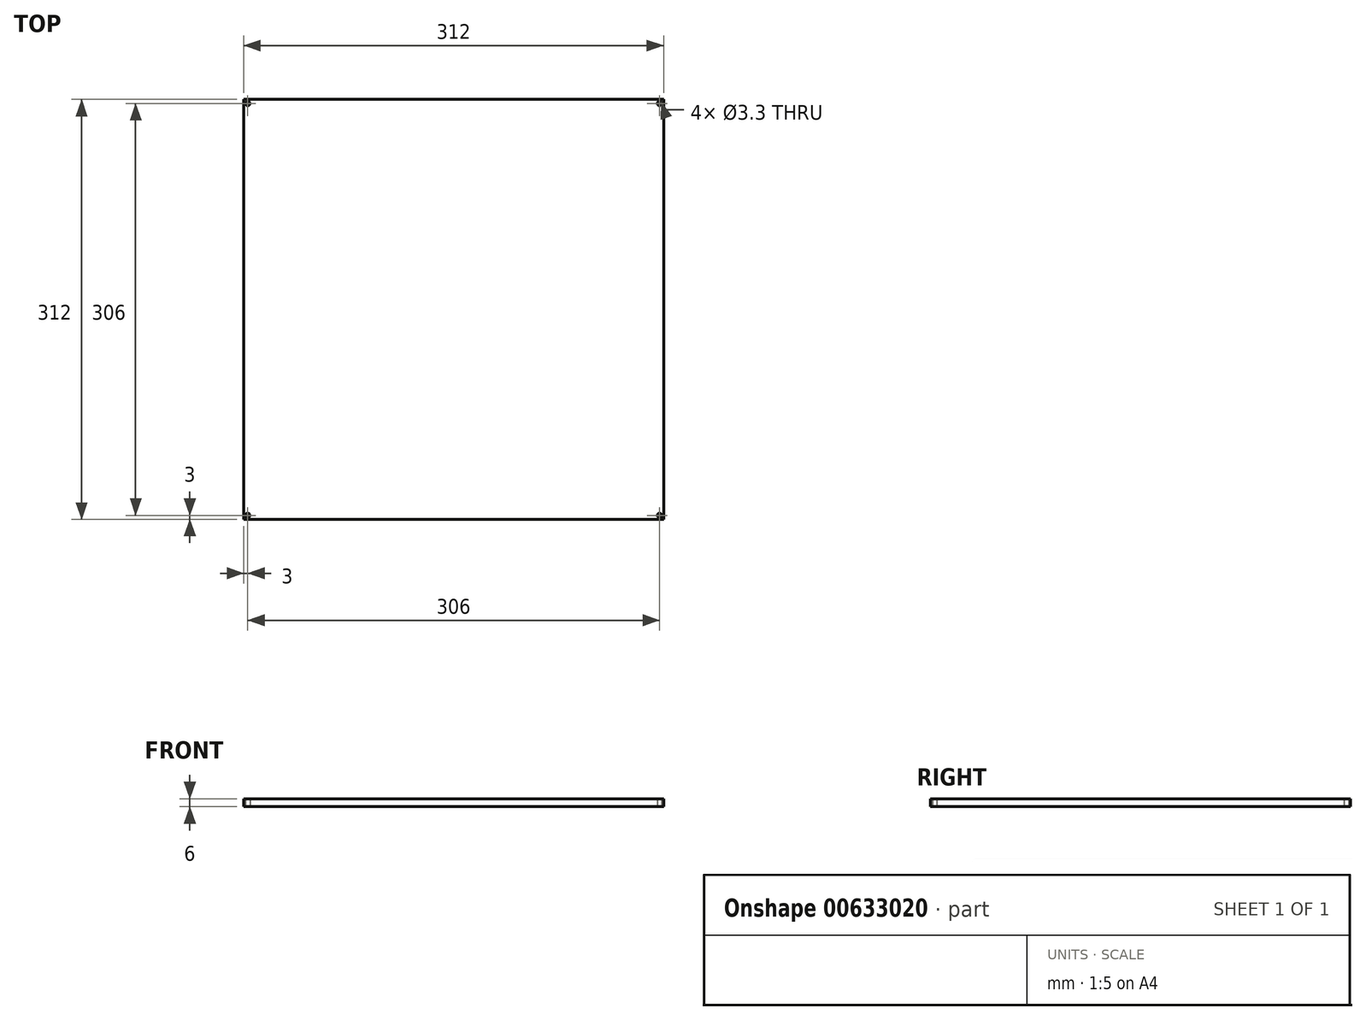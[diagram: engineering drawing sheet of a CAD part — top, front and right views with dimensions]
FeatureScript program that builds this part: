
annotation { "Feature Type Name" : "Feature", "Feature Type Description" : "" }
export const myFeature = defineFeature(function(context is Context, id is Id, definition is map)
    precondition{}
    {
        {
            var Q0;
            Q0=qCreatedBy(makeId("Top.planeOp"),FACE);
            var sketch = newSketch(context, id + "F0", { "sketchPlane" : qUnion([Q0])});
            skLineSegment(sketch, "E0.bottom", {"start": v(0, 0) * mm, "end": v(312, 0) * mm});
            skLineSegment(sketch, "E0.top", {"start": v(0, 312) * mm, "end": v(312, 312) * mm});
            skLineSegment(sketch, "E0.left", {"start": v(0, 0) * mm, "end": v(0, 312) * mm});
            skLineSegment(sketch, "E0.right", {"start": v(312, 0) * mm, "end": v(312, 312) * mm});
            skCircle(sketch, "E1", {"center": v(3, 309) * mm, "radius": 1.65 * mm});
            skCircle(sketch, "E2", {"center": v(309, 309) * mm, "radius": 1.65 * mm});
            skCircle(sketch, "E3", {"center": v(309, 3) * mm, "radius": 1.65 * mm});
            skCircle(sketch, "E4", {"center": v(3, 3) * mm, "radius": 1.65 * mm});
            skLineSegment(sketch, "E5", {"start": v(3, 309) * mm, "end": v(3, 312) * mm, "construction": true});
            skLineSegment(sketch, "E6", {"start": v(3, 309) * mm, "end": v(0, 309) * mm, "construction": true});
            skLineSegment(sketch, "E7", {"start": v(309, 309) * mm, "end": v(309, 312) * mm, "construction": true});
            skLineSegment(sketch, "E8", {"start": v(309, 309) * mm, "end": v(312, 309) * mm, "construction": true});
            skLineSegment(sketch, "E9", {"start": v(309, 3) * mm, "end": v(312, 3) * mm, "construction": true});
            skLineSegment(sketch, "E10", {"start": v(309, 3) * mm, "end": v(309, 0) * mm, "construction": true});
            skLineSegment(sketch, "E11", {"start": v(3, 3) * mm, "end": v(0, 3) * mm, "construction": true});
            skLineSegment(sketch, "E12", {"start": v(3, 3) * mm, "end": v(3, 0) * mm, "construction": true});
            skSolve(sketch);
        }
        {
            var Q0;
            Q0=qSketchRegion(id+"F0",true);
            extrude(context, id + "F1", {"entities" : qUnion([Q0]), "depth" : 6 * mm});
        }
    });
